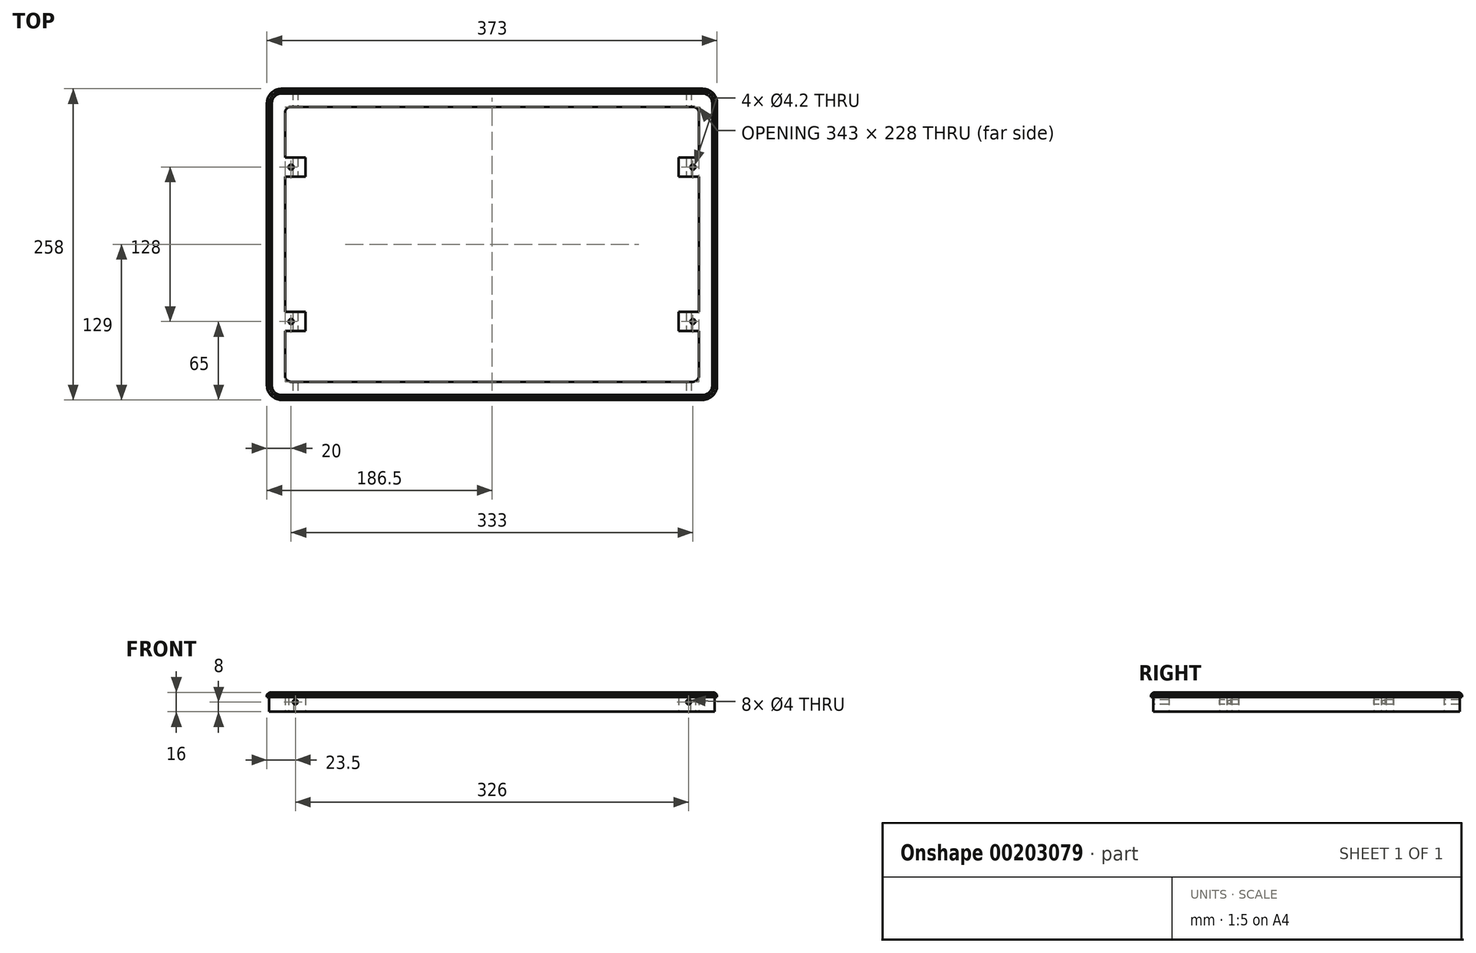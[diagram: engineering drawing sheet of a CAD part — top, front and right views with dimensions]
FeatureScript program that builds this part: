
annotation { "Feature Type Name" : "Feature", "Feature Type Description" : "" }
export const myFeature = defineFeature(function(context is Context, id is Id, definition is map)
    precondition{}
    {
        {
            var Q0;
            Q0=qCreatedBy(makeId("Top.planeOp"),FACE);
            var sketch = newSketch(context, id + "F0", { "sketchPlane" : qUnion([Q0])});
            skLineSegment(sketch, "E0.bottom", {"start": v(-174.5, 129) * mm, "end": v(174.5, 129) * mm});
            skLineSegment(sketch, "E0.top", {"start": v(-174.5, -129) * mm, "end": v(174.5, -129) * mm});
            skLineSegment(sketch, "E0.left", {"start": v(-186.5, 117) * mm, "end": v(-186.5, -117) * mm});
            skLineSegment(sketch, "E0.right", {"start": v(186.5, 117) * mm, "end": v(186.5, -117) * mm});
            skPoint(sketch, "E1.visualSharp", {"position": v(-186.5, -129) * mm});
            skArc(sketch, "E1.filletArc", {"start": v(-186.5, -117) * mm, "mid": v(-182.99, -125.49) * mm, "end": v(-174.5, -129) * mm});
            skPoint(sketch, "E2.visualSharp", {"position": v(-186.5, 129) * mm});
            skArc(sketch, "E2.filletArc", {"start": v(-174.5, 129) * mm, "mid": v(-182.99, 125.49) * mm, "end": v(-186.5, 117) * mm});
            skPoint(sketch, "E3.visualSharp", {"position": v(186.5, 129) * mm});
            skArc(sketch, "E3.filletArc", {"start": v(186.5, 117) * mm, "mid": v(182.99, 125.49) * mm, "end": v(174.5, 129) * mm});
            skPoint(sketch, "E4.visualSharp", {"position": v(186.5, -129) * mm});
            skArc(sketch, "E4.filletArc", {"start": v(174.5, -129) * mm, "mid": v(182.99, -125.49) * mm, "end": v(186.5, -117) * mm});
            skLineSegment(sketch, "E5.bottom", {"start": v(-166.5, 114) * mm, "end": v(166.5, 114) * mm});
            skLineSegment(sketch, "E5.top", {"start": v(-166.5, -114) * mm, "end": v(166.5, -114) * mm});
            skLineSegment(sketch, "E5.left", {"start": v(-171.5, 109) * mm, "end": v(-171.5, 72) * mm});
            skLineSegment(sketch, "E5.right", {"start": v(171.5, 109) * mm, "end": v(171.5, 72) * mm});
            skLineSegment(sketch, "E6.bottom", {"start": v(-171.5, 72) * mm, "end": v(-154.5, 72) * mm});
            skLineSegment(sketch, "E6.top", {"start": v(-171.5, 56) * mm, "end": v(-154.5, 56) * mm});
            skLineSegment(sketch, "E6.right", {"start": v(-154.5, 72) * mm, "end": v(-154.5, 56) * mm});
            skLineSegment(sketch, "E7.trimOffspring", {"start": v(-171.5, 56) * mm, "end": v(-171.5, -56) * mm});
            skLineSegment(sketch, "E8.MirrorCS", {"start": v(171.5, 72) * mm, "end": v(154.5, 72) * mm});
            skLineSegment(sketch, "E9.MirrorCS", {"start": v(154.5, 72) * mm, "end": v(154.5, 56) * mm});
            skLineSegment(sketch, "E10.MirrorCS", {"start": v(171.5, 56) * mm, "end": v(154.5, 56) * mm});
            skLineSegment(sketch, "E11.trimOffspring", {"start": v(171.5, 56) * mm, "end": v(171.5, -56) * mm});
            skLineSegment(sketch, "E12.MirrorCS", {"start": v(-171.5, -56) * mm, "end": v(-154.5, -56) * mm});
            skLineSegment(sketch, "E13.MirrorCS", {"start": v(-154.5, -72) * mm, "end": v(-154.5, -56) * mm});
            skLineSegment(sketch, "E14.MirrorCS", {"start": v(-171.5, -72) * mm, "end": v(-154.5, -72) * mm});
            skLineSegment(sketch, "E15.MirrorCS", {"start": v(171.5, -56) * mm, "end": v(154.5, -56) * mm});
            skLineSegment(sketch, "E16.MirrorCS", {"start": v(154.5, -72) * mm, "end": v(154.5, -56) * mm});
            skLineSegment(sketch, "E17.MirrorCS", {"start": v(171.5, -72) * mm, "end": v(154.5, -72) * mm});
            skLineSegment(sketch, "E18.trimOffspring", {"start": v(-171.5, -72) * mm, "end": v(-171.5, -109) * mm});
            skLineSegment(sketch, "E19.trimOffspring", {"start": v(171.5, -72) * mm, "end": v(171.5, -109) * mm});
            skCircle(sketch, "E20", {"center": v(-166.5, 64) * mm, "radius": 2.1 * mm});
            skCircle(sketch, "E21.MirrorC", {"center": v(166.5, 64) * mm, "radius": 2.1 * mm});
            skCircle(sketch, "E22.MirrorC", {"center": v(-166.5, -64) * mm, "radius": 2.1 * mm});
            skCircle(sketch, "E23.MirrorC", {"center": v(166.5, -64) * mm, "radius": 2.1 * mm});
            skPoint(sketch, "E24.MirrorCS.end.orphan", {"position": v(-154.5, -99) * mm});
            skPoint(sketch, "E25.orphan", {"position": v(-171.5, -99) * mm});
            skPoint(sketch, "E26.orphan", {"position": v(-154.5, -114) * mm});
            skPoint(sketch, "E27.top.end.orphan", {"position": v(-154.5, 99) * mm});
            skPoint(sketch, "E28.MirrorCS.end.orphan", {"position": v(154.5, 99) * mm});
            skPoint(sketch, "E29.MirrorCS.end.orphan", {"position": v(154.5, -99) * mm});
            skPoint(sketch, "E30.orphan", {"position": v(154.5, 114) * mm});
            skPoint(sketch, "E31.orphan", {"position": v(171.5, 99) * mm});
            skPoint(sketch, "E32.orphan", {"position": v(-154.5, 114) * mm});
            skPoint(sketch, "E33.orphan", {"position": v(-171.5, 99) * mm});
            skPoint(sketch, "E34.orphan", {"position": v(154.5, -114) * mm});
            skPoint(sketch, "E35.orphan", {"position": v(171.5, -99) * mm});
            skArc(sketch, "E36.filletArc", {"start": v(-166.5, 114) * mm, "mid": v(-170.04, 112.54) * mm, "end": v(-171.5, 109) * mm});
            skPoint(sketch, "E37.visualSharp", {"position": v(171.5, 114) * mm});
            skArc(sketch, "E37.filletArc", {"start": v(171.5, 109) * mm, "mid": v(170.04, 112.54) * mm, "end": v(166.5, 114) * mm});
            skPoint(sketch, "E38.visualSharp", {"position": v(171.5, -114) * mm});
            skArc(sketch, "E38.filletArc", {"start": v(166.5, -114) * mm, "mid": v(170.04, -112.54) * mm, "end": v(171.5, -109) * mm});
            skPoint(sketch, "E39.visualSharp", {"position": v(-171.5, -114) * mm});
            skArc(sketch, "E39.filletArc", {"start": v(-171.5, -109) * mm, "mid": v(-170.04, -112.54) * mm, "end": v(-166.5, -114) * mm});
            skSolve(sketch);
        }
        {
            var Q0;
            Q0=makeQuery(id+"F0.imprint","IMPRINT",FACE,{"disambiguationData":[TD([[makeQuery(id+"F0.imprint","IMPRINT",EDGE,{"derivedFrom":sQuery(id+"F0.wireOp",EDGE,"E0.bottom")}),-1.0]])]});
            extrude(context, id + "F1", {"entities" : qUnion([Q0]), "depth" : 16 * mm});
        }
        {
            var Q0;
            Q0=makeQuery(id+"F1.opExtrude","CAP_EDGE",EDGE,{"disambiguationData":[OSD([sQuery(id+"F0.wireOp",EDGE,"E0.top")])],"isStart":false});
            chamfer(context, id + "F2", {"entities" : qUnion([Q0]), "width" : 2 * mm, "tangentPropagation" : true});
        }
        {
            var Q0;
            Q0=makeQuery(id+"F1.opExtrude","CAP_FACE",FACE,{"disambiguationData":[OSD([sQuery(id+"F0.wireOp",EDGE,"E0.bottom"),sQuery(id+"F0.wireOp",EDGE,"E0.top"),sQuery(id+"F0.wireOp",EDGE,"E0.left"),sQuery(id+"F0.wireOp",EDGE,"E0.right"),sQuery(id+"F0.wireOp",EDGE,"E1.filletArc"),sQuery(id+"F0.wireOp",EDGE,"E2.filletArc"),sQuery(id+"F0.wireOp",EDGE,"E3.filletArc"),sQuery(id+"F0.wireOp",EDGE,"E4.filletArc"),sQuery(id+"F0.wireOp",EDGE,"E5.bottom"),sQuery(id+"F0.wireOp",EDGE,"E5.top"),sQuery(id+"F0.wireOp",EDGE,"E5.left"),sQuery(id+"F0.wireOp",EDGE,"E5.right")])],"isStart":false});
            var sketch = newSketch(context, id + "F3", { "sketchPlane" : qUnion([Q0])});
            skLineSegment(sketch, "E40.0", {"start": v(-182.5, 117) * mm, "end": v(-182.5, -117) * mm});
            skLineSegment(sketch, "E40.1", {"start": v(174.5, 125) * mm, "end": v(-174.5, 125) * mm});
            skLineSegment(sketch, "E40.2", {"start": v(182.5, -117) * mm, "end": v(182.5, 117) * mm});
            skLineSegment(sketch, "E40.3", {"start": v(-174.5, -125) * mm, "end": v(174.5, -125) * mm});
            skPoint(sketch, "E41.visualSharp", {"position": v(-182.5, -125) * mm});
            skArc(sketch, "E41.filletArc", {"start": v(-182.5, -117) * mm, "mid": v(-180.16, -122.66) * mm, "end": v(-174.5, -125) * mm});
            skPoint(sketch, "E42.visualSharp", {"position": v(-182.5, 125) * mm});
            skArc(sketch, "E42.filletArc", {"start": v(-174.5, 125) * mm, "mid": v(-180.16, 122.66) * mm, "end": v(-182.5, 117) * mm});
            skPoint(sketch, "E43.visualSharp", {"position": v(182.5, 125) * mm});
            skArc(sketch, "E43.filletArc", {"start": v(182.5, 117) * mm, "mid": v(180.16, 122.66) * mm, "end": v(174.5, 125) * mm});
            skPoint(sketch, "E44.visualSharp", {"position": v(182.5, -125) * mm});
            skArc(sketch, "E44.filletArc", {"start": v(174.5, -125) * mm, "mid": v(180.16, -122.66) * mm, "end": v(182.5, -117) * mm});
            skSolve(sketch);
        }
        {
            var Q0;
            Q0=qSketchRegion(id+"F3",true);
            extrude(context, id + "F4", {"entities" : qUnion([Q0]), "operationType" : NewBodyOperationType.REMOVE, "oppositeDirection" : true, "depth" : 3.1 * mm});
        }
        {
            var Q0;
            Q0=makeQuery(id+"F0.imprint","IMPRINT",FACE,{"disambiguationData":[TD([[makeQuery(id+"F0.imprint","IMPRINT",EDGE,{"derivedFrom":sQuery(id+"F0.wireOp",EDGE,"E0.bottom")}),-1.0]])]});
            var sketch = newSketch(context, id + "F5", { "sketchPlane" : qUnion([Q0])});
            skLineSegment(sketch, "E45.1", {"start": v(-172.6, 127.1) * mm, "end": v(172.6, 127.1) * mm});
            skLineSegment(sketch, "E45.2", {"start": v(-184.6, 115.1) * mm, "end": v(-184.6, -115.1) * mm});
            skLineSegment(sketch, "E45.5", {"start": v(-172.6, -127.1) * mm, "end": v(172.6, -127.1) * mm});
            skLineSegment(sketch, "E45.7", {"start": v(184.6, 115.1) * mm, "end": v(184.6, -115.1) * mm});
            skArc(sketch, "E46.filletArc", {"start": v(-184.6, -115.1) * mm, "mid": v(-181.09, -123.59) * mm, "end": v(-172.6, -127.1) * mm});
            skArc(sketch, "E47.filletArc", {"start": v(172.6, -127.1) * mm, "mid": v(181.09, -123.59) * mm, "end": v(184.6, -115.1) * mm});
            skArc(sketch, "E48.filletArc", {"start": v(184.6, 115.1) * mm, "mid": v(181.09, 123.59) * mm, "end": v(172.6, 127.1) * mm});
            skArc(sketch, "E49.filletArc", {"start": v(-172.6, 127.1) * mm, "mid": v(-181.09, 123.59) * mm, "end": v(-184.6, 115.1) * mm});
            skArc(sketch, "E50.0", {"start": v(-172.6, 132.1) * mm, "mid": v(-184.62, 127.12) * mm, "end": v(-189.6, 115.1) * mm});
            skLineSegment(sketch, "E50.1", {"start": v(-172.6, 132.1) * mm, "end": v(172.6, 132.1) * mm});
            skLineSegment(sketch, "E50.2", {"start": v(-189.6, 115.1) * mm, "end": v(-189.6, -115.1) * mm});
            skArc(sketch, "E50.3", {"start": v(189.6, 115.1) * mm, "mid": v(184.62, 127.12) * mm, "end": v(172.6, 132.1) * mm});
            skArc(sketch, "E50.4", {"start": v(-189.6, -115.1) * mm, "mid": v(-184.62, -127.12) * mm, "end": v(-172.6, -132.1) * mm});
            skLineSegment(sketch, "E50.5", {"start": v(-172.6, -132.1) * mm, "end": v(172.6, -132.1) * mm});
            skArc(sketch, "E50.6", {"start": v(172.6, -132.1) * mm, "mid": v(184.62, -127.12) * mm, "end": v(189.6, -115.1) * mm});
            skLineSegment(sketch, "E50.7", {"start": v(189.6, 115.1) * mm, "end": v(189.6, -115.1) * mm});
            skSolve(sketch);
        }
        {
            var Q0;
            Q0=qSketchRegion(id+"F5",true);
            extrude(context, id + "F6", {"entities" : qUnion([Q0]), "operationType" : NewBodyOperationType.REMOVE, "depth" : 12 * mm});
        }
        {
            var Q0;
            Q0=makeQuery(id+"F6.boolean.opBoolean","COPY",FACE,{"derivedFrom":makeQuery(id+"F6.opExtrude","SWEPT_FACE",FACE,{"disambiguationData":[OSD([sQuery(id+"F5.wireOp",EDGE,"E45.5")])]})});
            var sketch = newSketch(context, id + "F7", { "sketchPlane" : qUnion([Q0])});
            skCircle(sketch, "E51", {"center": v(-163, 8) * mm, "radius": 2 * mm});
            skCircle(sketch, "E52.MirrorC", {"center": v(163, 8) * mm, "radius": 2 * mm});
            skSolve(sketch);
        }
        {
            var Q0;
            Q0=qSketchRegion(id+"F7",true);
            extrude(context, id + "F8", {"entities" : qUnion([Q0]), "operationType" : NewBodyOperationType.REMOVE, "endBound" : BoundingType.THROUGH_ALL, "oppositeDirection" : true, "depth" : 25 * mm});
        }
    });
